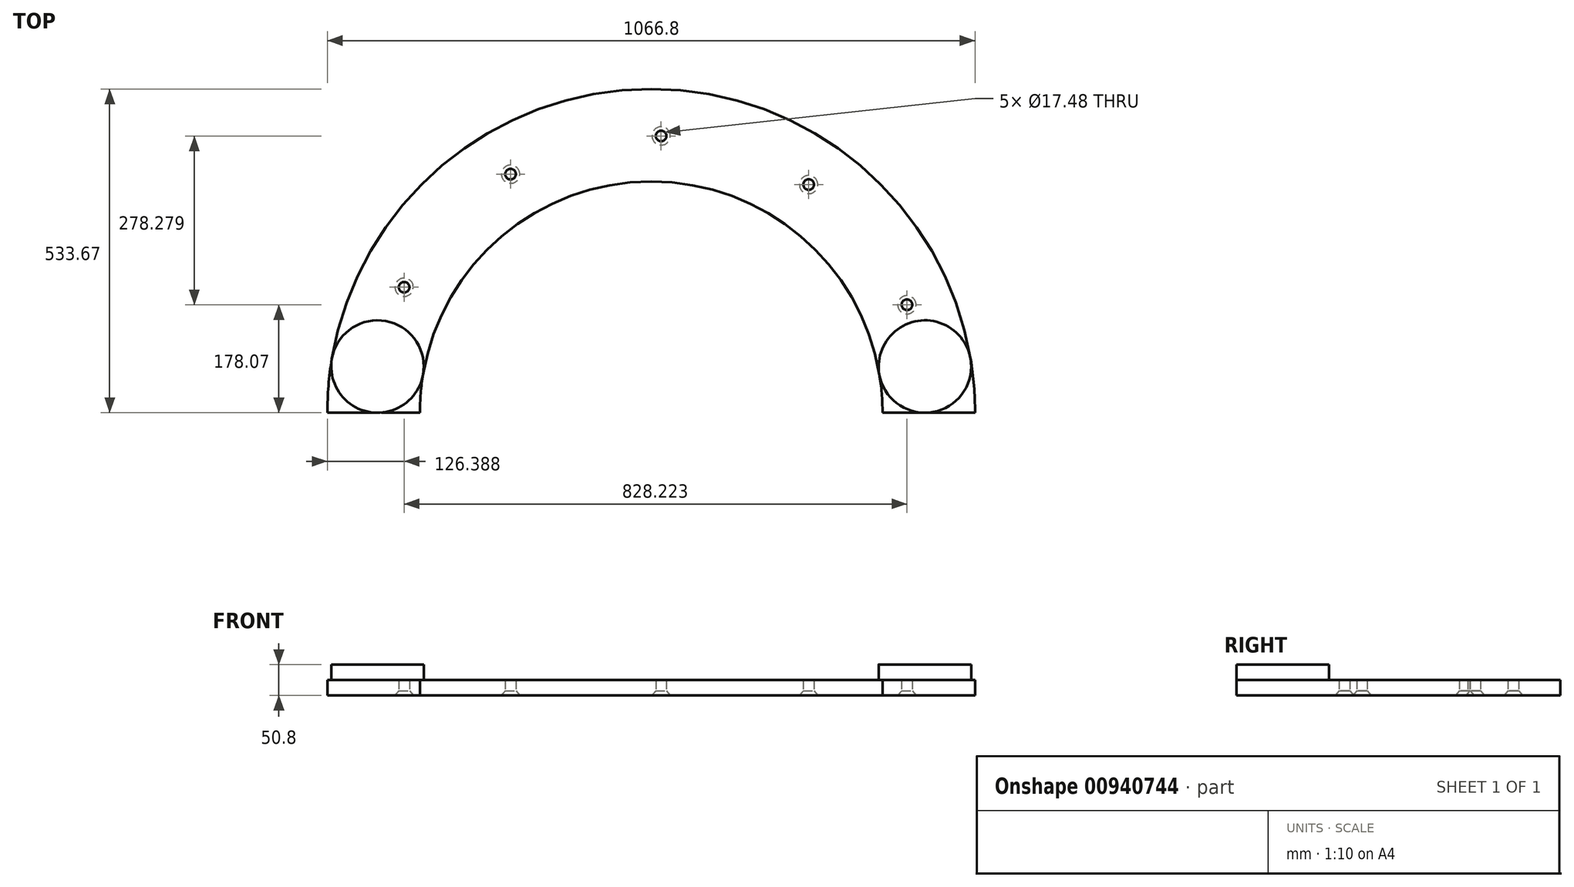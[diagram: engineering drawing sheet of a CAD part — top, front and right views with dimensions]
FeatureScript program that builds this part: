
annotation { "Feature Type Name" : "Feature", "Feature Type Description" : "" }
export const myFeature = defineFeature(function(context is Context, id is Id, definition is map)
    precondition{}
    {
        {
            var Q0;
            Q0=qCreatedBy(makeId("Top.planeOp"),FACE);
            var sketch = newSketch(context, id + "F0", { "sketchPlane" : qUnion([Q0])});
            skArc(sketch, "E0", {"start": v(-533.4, 0) * mm, "mid": v(0, 533.4) * mm, "end": v(533.4, 0) * mm});
            skArc(sketch, "E1", {"start": v(-381, 0) * mm, "mid": v(0, 381) * mm, "end": v(381, 0) * mm});
            skLineSegment(sketch, "E2", {"start": v(-533.4, 0) * mm, "end": v(-381, 0) * mm});
            skLineSegment(sketch, "E3", {"start": v(381, 0) * mm, "end": v(533.4, 0) * mm});
            skSolve(sketch);
        }
        {
            var Q0;
            Q0 = qSketchRegion(id + "F0", true);
            extrude(context, id + "F1", {"entities" : qUnion([Q0]), "depth" : 25.4 * mm, "offsetDistance" : 25.4 * mm});
        }
        {
            var Q0;
            Q0=makeQuery(id+"F1.opExtrude","CAP_FACE",FACE,{"disambiguationData":[OSD([sQuery(id+"F0.wireOp",EDGE,"E0"),sQuery(id+"F0.wireOp",EDGE,"E1"),sQuery(id+"F0.wireOp",EDGE,"E2"),sQuery(id+"F0.wireOp",EDGE,"E3")])],"isStart":false});
            var sketch = newSketch(context, id + "F2", { "sketchPlane" : qUnion([Q0])});
            skCircle(sketch, "E4", {"center": v(-450.85, 75.93) * mm, "radius": 76.2 * mm});
            skPoint(sketch, "E4.first.point", {"position": v(-457.2, 0) * mm});
            skPoint(sketch, "E4.second.point", {"position": v(-457.2, 151.87) * mm});
            skPoint(sketch, "E4.second.point.positionSnap0", {"position": v(-457.2, 0) * mm});
            skPoint(sketch, "E4.third.point", {"position": v(-375.7, 63.28) * mm});
            skLineSegment(sketch, "E5", {"start": v(0, 0) * mm, "end": v(0, 381) * mm, "construction": true});
            skCircle(sketch, "E6.MirrorC", {"center": v(450.85, 75.93) * mm, "radius": 76.2 * mm});
            skSolve(sketch);
        }
        {
            var Q0;
            Q0 = qSketchRegion(id + "F2", true);
            extrude(context, id + "F3", {"entities" : qUnion([Q0]), "operationType" : NewBodyOperationType.ADD, "depth" : 25.4 * mm, "offsetDistance" : 25.4 * mm});
        }
        {
            var Q0;
            Q0=makeQuery(id+"F1.opExtrude","CAP_FACE",FACE,{"disambiguationData":[OSD([sQuery(id+"F0.wireOp",EDGE,"E0"),sQuery(id+"F0.wireOp",EDGE,"E1"),sQuery(id+"F0.wireOp",EDGE,"E2"),sQuery(id+"F0.wireOp",EDGE,"E3")])],"isStart":true});
            var sketch = newSketch(context, id + "F4", { "sketchPlane" : qUnion([Q0])});
            skArc(sketch, "E7", {"start": v(-457.2, 0) * mm, "mid": v(0, -457.2) * mm, "end": v(457.2, 0) * mm});
            skPoint(sketch, "E8", {"position": v(421.21, -177.8) * mm});
            skPoint(sketch, "E9.1.0", {"position": v(259.32, -375.95) * mm});
            skPoint(sketch, "E9.2.0", {"position": v(16.31, -456.08) * mm});
            skPoint(sketch, "E9.3.0", {"position": v(-231.7, -393.1) * mm});
            skPoint(sketch, "E9.4.0", {"position": v(-407.01, -206.72) * mm});
            skPoint(sketch, "E9.center", {"position": v(0.36, 0.84) * mm});
            skLineSegment(sketch, "E9.anchor1", {"start": v(0.36, 0.84) * mm, "end": v(421.21, -177.8) * mm, "construction": true});
            skLineSegment(sketch, "E9.anchor2", {"start": v(0.36, 0.84) * mm, "end": v(-407.01, -206.72) * mm, "construction": true});
            skSolve(sketch);
        }
        {
            var Q0;
            Q0=sQuery(id+"F4.wireOp",VERTEX,"E9.4.0");
            var Q1;
            Q1=sQuery(id+"F4.wireOp",VERTEX,"E9.3.0");
            var Q2;
            Q2=sQuery(id+"F4.wireOp",VERTEX,"E9.2.0");
            var Q3;
            Q3=sQuery(id+"F4.wireOp",VERTEX,"E9.1.0");
            var Q4;
            Q4=sQuery(id+"F4.wireOp",VERTEX,"E8");
            var Q5;
            Q5=makeQuery(id+"F1.opExtrude","SWEPT_BODY",BODY,{"disambiguationData":[OSD([sQuery(id+"F0.wireOp",EDGE,"E0"),sQuery(id+"F0.wireOp",EDGE,"E1"),sQuery(id+"F0.wireOp",EDGE,"E2"),sQuery(id+"F0.wireOp",EDGE,"E3")])]});
            hole(context, id + "F5", {"style" : HoleStyle.C_SINK, "endStyle" : HoleEndStyle.THROUGH, "standardTappedOrClearance" : lookupTablePath({ "fit" : "Normal (ASME)", "standard" : "ANSI", "size" : "5/8", "type" : "Clearance" }), "standardBlindInLast" : lookupTablePath({ "fit" : "Normal", "standard" : "ANSI", "engagement" : "75%", "pitch" : "11 tpi", "size" : "5/8", "type" : "Clearance & tapped" }), "holeDiameter" : 17.48 * mm, "cSinkDiameter" : 30.18 * mm, "cSinkAngle" : 82 * degree, "majorDiameter" : 6.35 * mm, "isTappedThrough" : true, "tappedDepth" : 12.7 * mm, "tapClearance" : 3, "locations" : qUnion([Q0, Q1, Q2, Q3, Q4]), "scope" : qUnion([Q5])});
        }
    });
